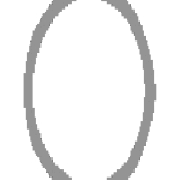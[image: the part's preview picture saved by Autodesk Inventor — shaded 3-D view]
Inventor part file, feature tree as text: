
AUTODESK INVENTOR PART (.ipt)
format: ipt  version: 2021 (Build 250183000, 183)  size: 112,640 bytes
history: native  units: in
note: dims shown in document units (in); Inventor stores cm internally (conversion verified against a paired STEP export)
features: other x4, sketch x3, plane x1
ambient origin geometry x8: Origin, YZ Plane, XZ Plane, XY Plane, X Axis, Y Axis, Z Axis, Center Point
bodies: Solid1 (feature_tree), Body (feature_tree)
feature tree (8):
  other  "Driven Length"
  other  "Frame Generator"
  other  "Start Plane"
  other  "End Plane"
  sketch  "Sketch"  dims[d2=26.4998in d4=-0.0in d5=26.4998in d6=0.12in d7=0.0in d8=90.0deg d9=26.4998in]
  sketch  "Sketch2"  dims[d0=1.0in]
  plane  "Work Plane3"
  sketch  "Sketch3"  dims[d1=0.065in]
